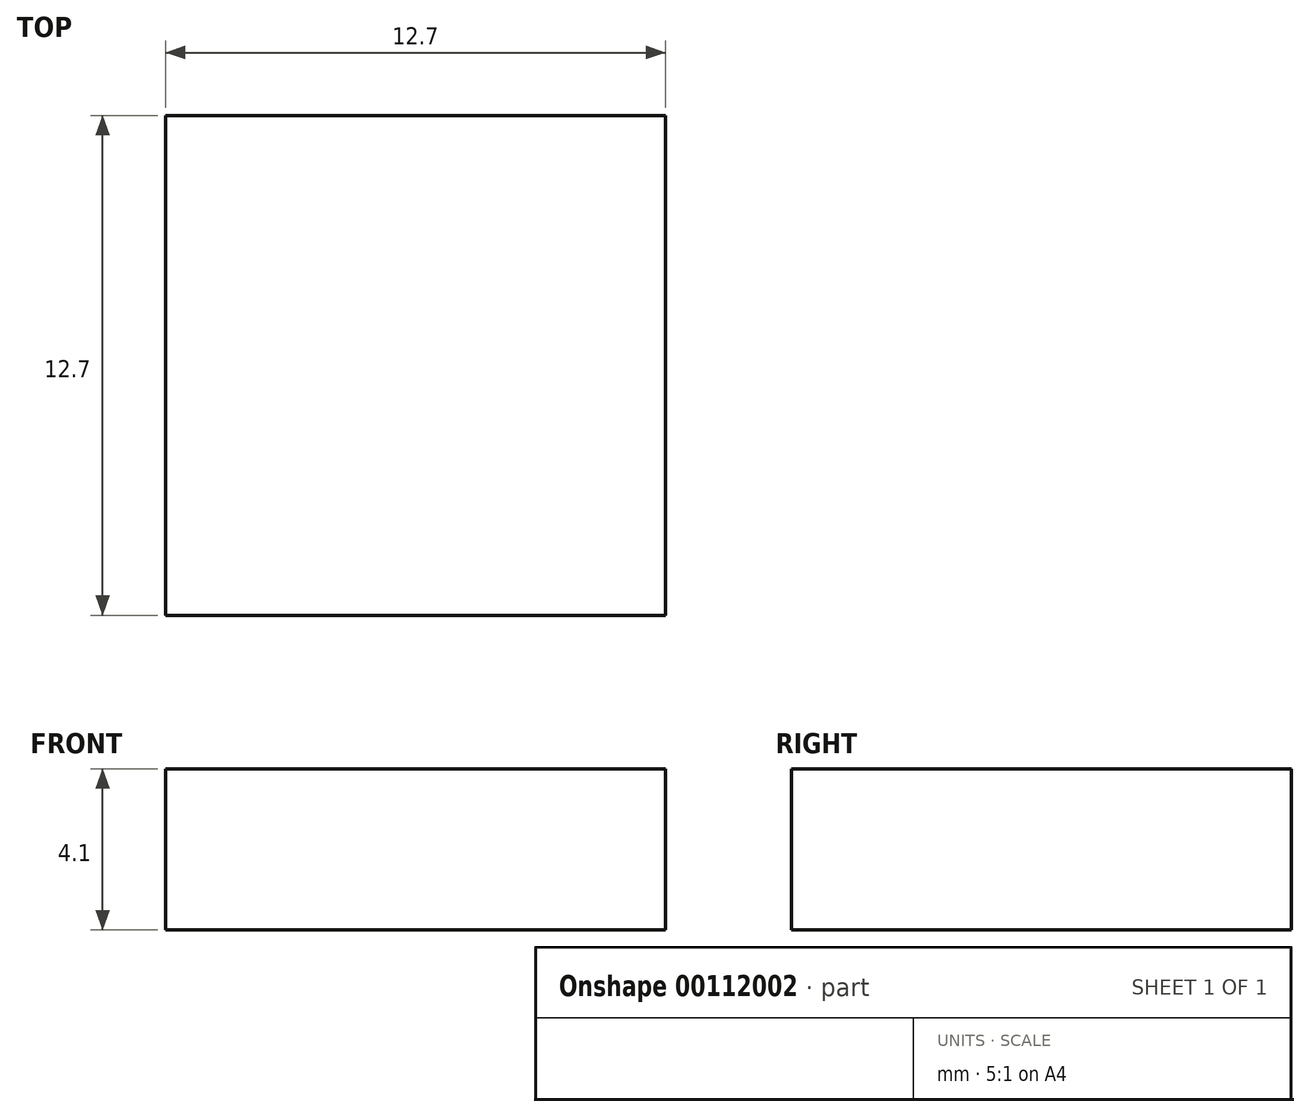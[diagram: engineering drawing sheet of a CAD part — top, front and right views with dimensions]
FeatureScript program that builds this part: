
annotation { "Feature Type Name" : "Feature", "Feature Type Description" : "" }
export const myFeature = defineFeature(function(context is Context, id is Id, definition is map)
    precondition{}
    {
        {
            var Q0;
            Q0=qCreatedBy(makeId("Top.planeOp"),FACE);
            var sketch = newSketch(context, id + "F0", { "sketchPlane" : qUnion([Q0])});
            skLineSegment(sketch, "E0.bottom", {"start": v(0, 0) * mm, "end": v(12.7, 0) * mm});
            skLineSegment(sketch, "E0.top", {"start": v(0, -12.7) * mm, "end": v(12.7, -12.7) * mm});
            skLineSegment(sketch, "E0.left", {"start": v(0, 0) * mm, "end": v(0, -12.7) * mm});
            skLineSegment(sketch, "E0.right", {"start": v(12.7, 0) * mm, "end": v(12.7, -12.7) * mm});
            skSolve(sketch);
        }
        {
            var Q0;
            Q0 = qSketchRegion(id + "F0", true);
            extrude(context, id + "F1", {"entities" : qUnion([Q0]), "depth" : 4.1 * mm});
        }
    });
